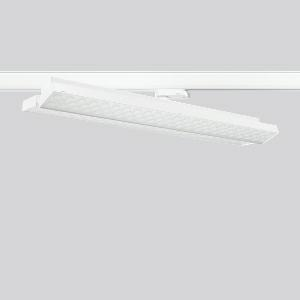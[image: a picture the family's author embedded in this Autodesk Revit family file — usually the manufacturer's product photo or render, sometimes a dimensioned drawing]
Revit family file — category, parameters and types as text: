
# Revit family: tx-move_742162_002_1_d8b9
name_source: partatom
category: Lighting Fixtures
units: mm (PartAtom-declared; Revit-internal decimal feet)

## family parameters
Cut with Voids When Loaded = No
Host = Face
Light Source = No
Part Type = Normal
Room Calculation Point = No
Round Connector Dimension = Use Diameter
Shared = No

## types (1)
- MultiLumen 1 (1 x LED Modul 840, 3150 lm, 4000)
    Apparent Load = 41 VA
    CIE Flux Codes = 77 96 99 100 100
    Color Rendering = 80
    Color Temperature = 4000
    Default Elevation = 1800 mm
    Description = Series: TX-MOVE
Multifunctional surface-mounted spotlight for area lighting. Very flat design. Housing: sheet steel, powder-coated. Rotation range: 356°. Swivel range: 90°. Consistent alignment possible with visible tilt scale. High-efficiency LED units with optimum light control thanks to clear plastic (PC) lens optics. Spezielle Mikrostrukturen reduzieren Gelbsaum. Symmetrical light distribution. With multi adaptor for 3-circuit tracks 230 V. Suitable for Track on ceiling. MultiLumen: Luminous flux adjustable in 3 steps. Factory setting is the highest luminous flux. Environmentally friendly and resource-saving due to replaceable and recyclable components. 
Colour: traffic white, matt (RAL 9016)
Length: 570 mm
Width: 119 mm
Height: 92 mm
Lamp: LED
Socket: without socket
Colour temperature: 4000K
Colour rendering index (CRI): 80
System power: 41 W
Rated luminous flux: 6300 lm
Luminous efficiency: 154 lm/W
System power 2: 57 W
Rated luminous flux 2: 8550 lm
Luminous efficiency 2: 150 lm/W
System power 3: 73 W
Rated luminous flux 3: 10400 lm
Luminous efficiency 3: 142 lm/W
Control gear: Regulated power supply
Protection class: I
Type of protection: IP 20
    Height = 75 mm
    Lamp = 1 x LED Modul 840
    Lamp Light Flux = 3150 lm
    Lamp count = 1
    Length = 569 mm
    Lifetime = 50000 h
    Luminous efficacy = 154 lm/W
    Manufacturer = RZB
    ModVariant = No
    Model = 742162.002.1
    Mounting Place = Ceiling
    Mounting Type = Surface mounted
    Number of Poles = 1
    OnlyDefault = Yes
    Power Factor = 1
    Product Name = TX-MOVE
    Product group = Track mounted projectors
    ProductGroupID = 301
    Protection Class = Protection class I
    Protection Degree = IP 20
    RLX_Detail_Level = 1
    RLX_Emergency_Light_Flux = 0 lm
    RLX_Emergency_Type = 0
    RLX_Emergency_Type_DB = No
    RlxData = <blob elided: 30973 chars, md5=2a3fe322>
    Socket = socket
    Standby Power = 0 W
    System Light Flux = 6300 lm
    System Power = 41 W
    Type Comments = MultiLumen 1
    Type Image = 742162.002.jpg
    URL = http://relux.com
    VarID = multilumen_1
    Voltage = 0 V
    Weight = 0.00 kg
    Width = 119 mm

## geometry (parser evidence)
native form markers: Blend x4, Sweep x14
no freeform markers — native parametric forms only
